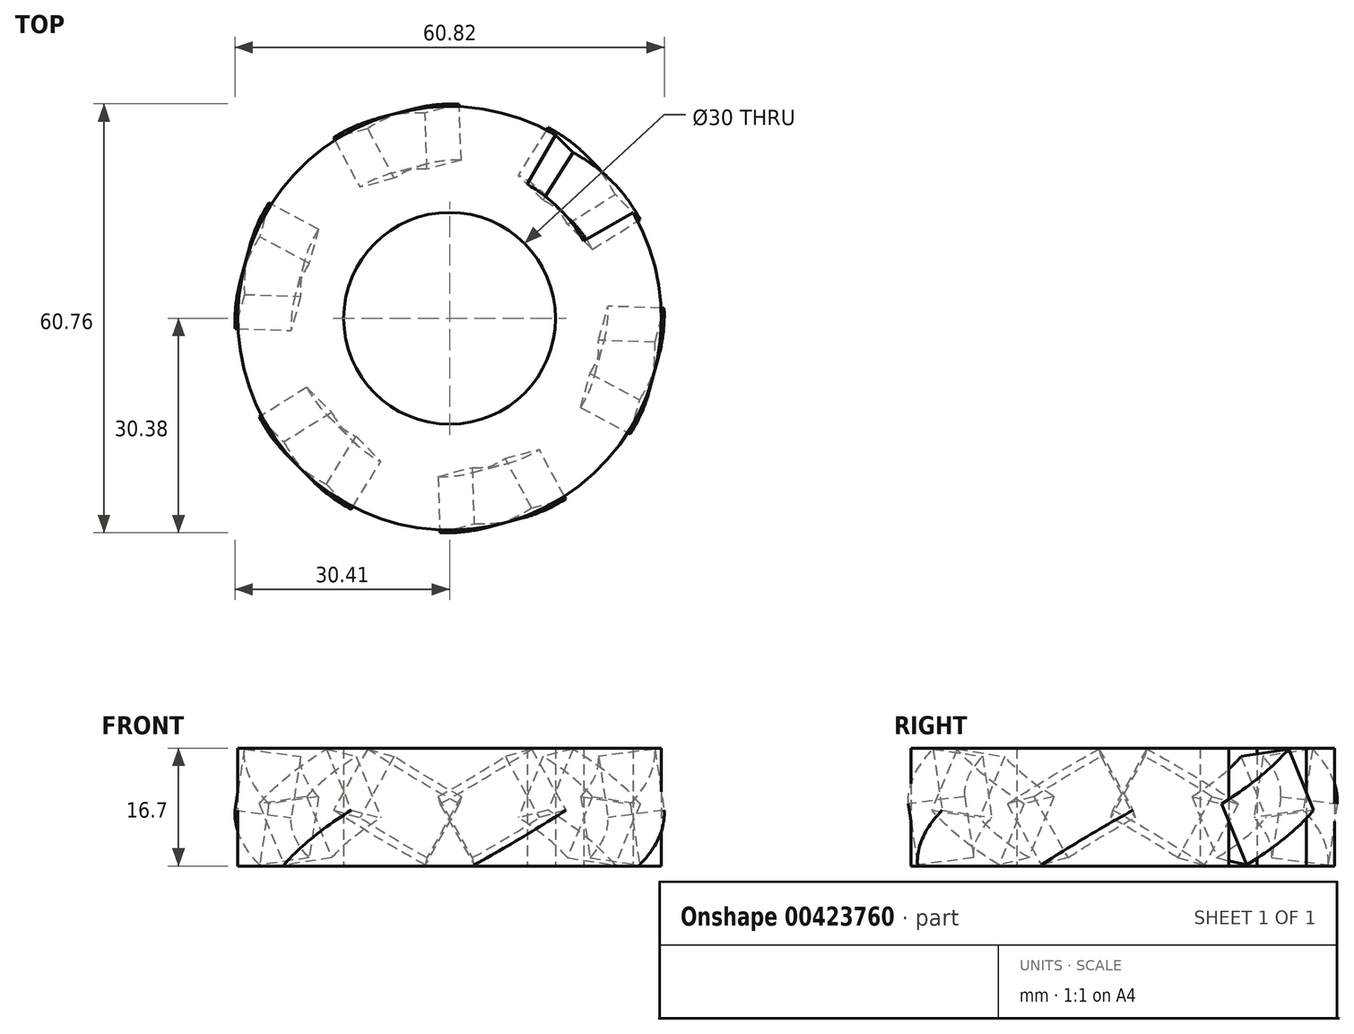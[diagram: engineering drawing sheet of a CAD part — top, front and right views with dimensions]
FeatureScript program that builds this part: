
annotation { "Feature Type Name" : "Feature", "Feature Type Description" : "" }
export const myFeature = defineFeature(function(context is Context, id is Id, definition is map)
    precondition{}
    {
        {
            var Q0;
            Q0=qCreatedBy(makeId("Top.planeOp"),FACE);
            var sketch = newSketch(context, id + "F0", { "sketchPlane" : qUnion([Q0])});
            skCircle(sketch, "E0", {"center": v(0, 0) * mm, "radius": 30 * mm});
            skCircle(sketch, "E1", {"center": v(0, 0) * mm, "radius": 15 * mm});
            skLineSegment(sketch, "E2.11.0", {"start": v(36.54, 63.3) * mm, "end": v(10.98, 19.02) * mm});
            skLineSegment(sketch, "E3.trimOffspring", {"start": v(36.54, 63.3) * mm, "end": v(50, 86.6) * mm});
            skPoint(sketch, "E4.orphan", {"position": v(63.3, 36.54) * mm});
            skArc(sketch, "E5", {"start": v(86.6, 50) * mm, "mid": v(70.71, 70.71) * mm, "end": v(50, 86.6) * mm});
            skLineSegment(sketch, "E6.trimOffspring", {"start": v(10.98, 19.02) * mm, "end": v(15, 25.98) * mm});
            skLineSegment(sketch, "E7.trimOffspring", {"start": v(19.02, 10.98) * mm, "end": v(86.6, 50) * mm});
            skArc(sketch, "E8", {"start": v(19.02, 10.98) * mm, "mid": v(15.53, 15.53) * mm, "end": v(10.98, 19.02) * mm});
            skSolve(sketch);
        }
        {
            var Q0;
            {var subQ1=sQuery(id+"F0.wireOp",EDGE,"E2.11.0");Q0=makeQuery(id+"F0.imprint","IMPRINT",FACE,{"disambiguationData":[TD([[makeQuery(id+"F0.imprint","IMPRINT",EDGE,{"derivedFrom":subQ1}),1.0]])]});}
            var Q1;
            {var subQ0=sQuery(id+"F0.wireOp",EDGE,"E6.trimOffspring");Q1=makeQuery(id+"F0.imprint","IMPRINT",FACE,{"disambiguationData":[TD([[makeQuery(id+"F0.imprint","IMPRINT",EDGE,{"derivedFrom":subQ0}),-1.0]])]});}
            extrude(context, id + "F1", {"entities" : qUnion([Q0, Q1]), "depth" : 10 * mm});
        }
        {
            var Q0;
            Q0=qCreatedBy(makeId("Top.planeOp"),FACE);
            cPlane(context, id + "F2", {"entities" : qUnion([Q0]), "cplaneType" : CPlaneType.OFFSET, "offset" : 5 * mm, "width" : 150 * mm, "height" : 150 * mm});
        }
        {
            var Q0;
            Q0=qCreatedBy(id+"F2.planeOp",FACE);
            var sketch = newSketch(context, id + "F3", { "sketchPlane" : qUnion([Q0])});
            skLineSegment(sketch, "E9.0.0", {"start": v(50, 86.6) * mm, "end": v(10.98, 19.02) * mm});
            skLineSegment(sketch, "E10", {"start": v(70.71, 70.71) * mm, "end": v(12.96, 13.43) * mm});
            skSolve(sketch);
        }
        {
            var Q0;
            Q0=makeQuery(id+"F1.opExtrude","SWEPT_BODY",BODY,{"disambiguationData":[OSD([sQuery(id+"F0.wireOp",EDGE,"E1"),sQuery(id+"F0.wireOp",EDGE,"E2.11.0"),sQuery(id+"F0.wireOp",EDGE,"E3.trimOffspring"),sQuery(id+"F0.wireOp",EDGE,"E5"),sQuery(id+"F0.wireOp",EDGE,"E6.trimOffspring"),sQuery(id+"F0.wireOp",EDGE,"E7.trimOffspring")])]});
            var Q1;
            Q1=sQuery(id+"F3.wireOp",EDGE,"E10");
            transform(context, id + "F4", {"entities" : qUnion([Q0]), "transformType" : TransformType.ROTATION, "transformAxis" : qUnion([Q1]), "angle" : 30 * degree, "oppositeDirection" : true, "makeCopy" : false});
        }
        {
            var Q0;
            Q0=qCreatedBy(makeId("Front.planeOp"),FACE);
            var sketch = newSketch(context, id + "F5", { "sketchPlane" : qUnion([Q0])});
            skLineSegment(sketch, "E11", {"start": v(0, 79.2) * mm, "end": v(0, -90.03) * mm});
            skSolve(sketch);
        }
        {
            var Q0;
            Q0=makeQuery(id+"F1.opExtrude","SWEPT_BODY",BODY,{"disambiguationData":[OSD([sQuery(id+"F0.wireOp",EDGE,"E1"),sQuery(id+"F0.wireOp",EDGE,"E2.11.0"),sQuery(id+"F0.wireOp",EDGE,"E3.trimOffspring"),sQuery(id+"F0.wireOp",EDGE,"E5"),sQuery(id+"F0.wireOp",EDGE,"E6.trimOffspring"),sQuery(id+"F0.wireOp",EDGE,"E7.trimOffspring")])]});
            var Q1;
            Q1=sQuery(id+"F5.wireOp",EDGE,"E11");
            circularPattern(context, id + "F6", {"entities" : qUnion([Q0]), "axis" : qUnion([Q1]), "angle" : 360 * degree, "instanceCount" : 6, "equalSpace" : true});
        }
        {
            var Q0;
            {var subQ0=sQuery(id+"F0.wireOp",EDGE,"E6.trimOffspring");Q0=makeQuery(id+"F0.imprint","IMPRINT",FACE,{"disambiguationData":[TD([[makeQuery(id+"F0.imprint","IMPRINT",EDGE,{"derivedFrom":subQ0}),-1.0]])]});}
            var Q1;
            Q1=makeQuery(id+"F0.imprint","IMPRINT",FACE,{"disambiguationData":[TD([[makeQuery(id+"F0.imprint","IMPRINT",EDGE,{"derivedFrom":sQuery(id+"F0.wireOp",EDGE,"E1")}),-1.0]])]});
            extrude(context, id + "F7", {"entities" : qUnion([Q0, Q1]), "depth" : 13.2 * mm, "hasSecondDirection" : true, "secondDirectionOppositeDirection" : true, "secondDirectionDepth" : 3.5 * mm});
        }
    });
